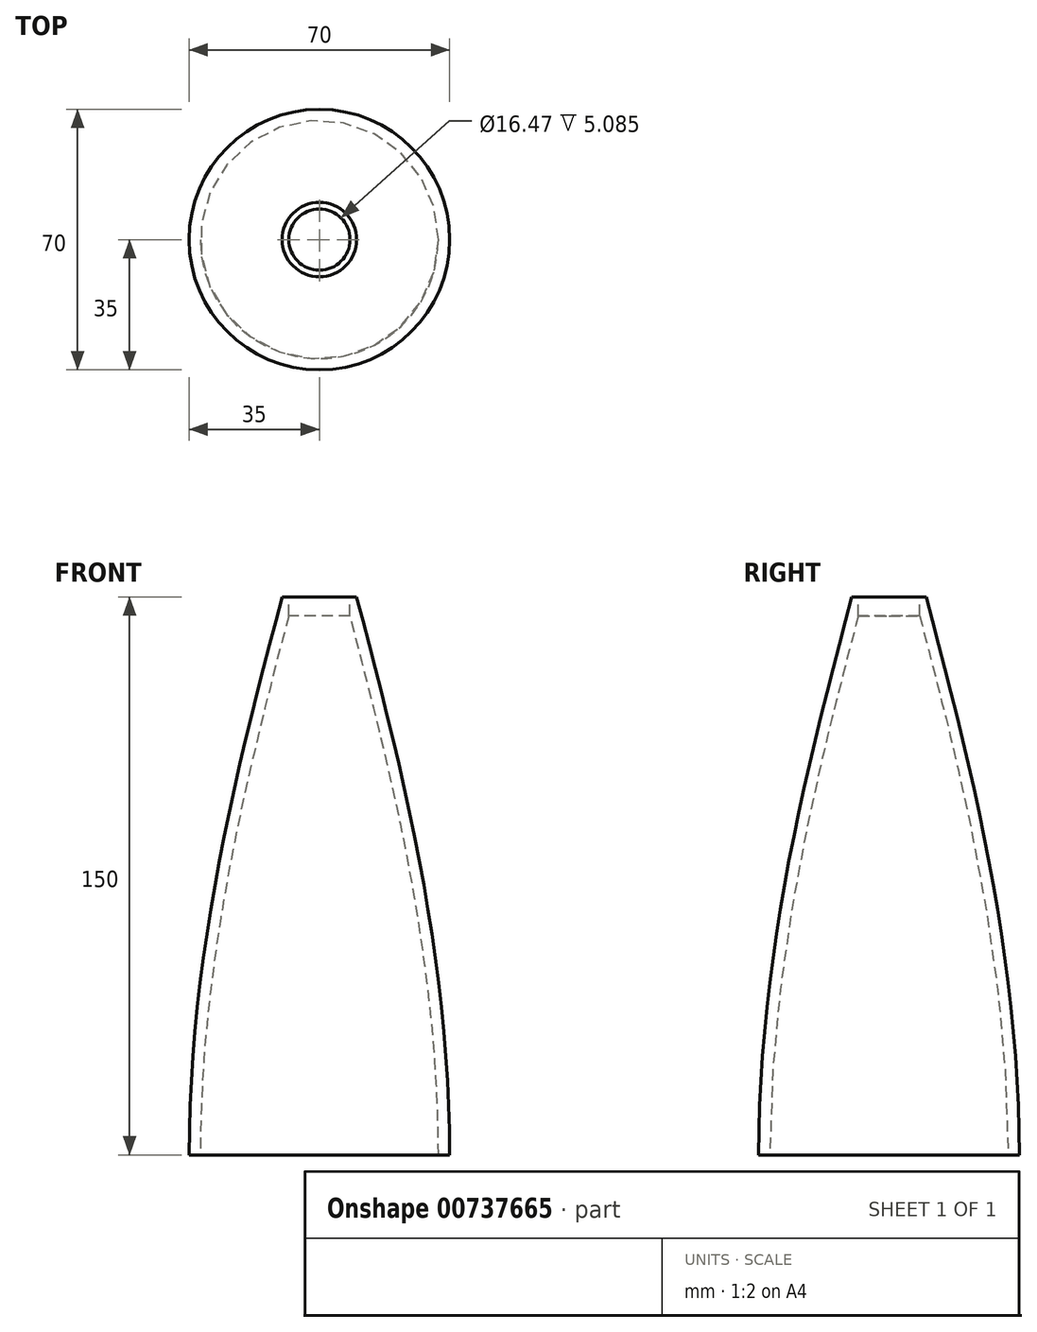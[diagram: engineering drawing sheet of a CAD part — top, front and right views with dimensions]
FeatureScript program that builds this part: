
annotation { "Feature Type Name" : "Feature", "Feature Type Description" : "" }
export const myFeature = defineFeature(function(context is Context, id is Id, definition is map)
    precondition{}
    {
        {
            var Q0;
            Q0=qCreatedBy(makeId("Top.planeOp"),FACE);
            var sketch = newSketch(context, id + "F0", { "sketchPlane" : qUnion([Q0])});
            skCircle(sketch, "E0", {"center": v(0, 0) * mm, "radius": 35 * mm});
            skSolve(sketch);
        }
        {
            var Q0;
            Q0=qCreatedBy(makeId("Top.planeOp"),FACE);
            cPlane(context, id + "F1", {"entities" : qUnion([Q0]), "cplaneType" : CPlaneType.OFFSET, "offset" : 100 * mm, "width" : 150 * mm, "height" : 150 * mm});
        }
        {
            var Q0;
            Q0=qCreatedBy(id+"F1.planeOp",FACE);
            var sketch = newSketch(context, id + "F2", { "sketchPlane" : qUnion([Q0])});
            skCircle(sketch, "E1", {"center": v(0, 0) * mm, "radius": 22.5 * mm});
            skSolve(sketch);
        }
        {
            var Q0;
            Q0=qCreatedBy(id+"F1.planeOp",FACE);
            cPlane(context, id + "F3", {"entities" : qUnion([Q0]), "cplaneType" : CPlaneType.OFFSET, "offset" : 50 * mm, "width" : 150 * mm, "height" : 150 * mm});
        }
        {
            var Q0;
            Q0=qCreatedBy(id+"F3.planeOp",FACE);
            var sketch = newSketch(context, id + "F4", { "sketchPlane" : qUnion([Q0])});
            skCircle(sketch, "E2", {"center": v(0, 0) * mm, "radius": 10 * mm});
            skSolve(sketch);
        }
        {
            var Q0;
            Q0=makeQuery(id+"F0.imprint","IMPRINT",FACE,{"disambiguationData":[TD([[makeQuery(id+"F0.imprint","IMPRINT",EDGE,{"derivedFrom":sQuery(id+"F0.wireOp",EDGE,"E0")}),1.0]])]});
            var Q1;
            Q1=makeQuery(id+"F2.imprint","IMPRINT",FACE,{"disambiguationData":[TD([[makeQuery(id+"F2.imprint","IMPRINT",EDGE,{"derivedFrom":sQuery(id+"F2.wireOp",EDGE,"E1")}),1.0]])]});
            var Q2;
            Q2=makeQuery(id+"F4.imprint","IMPRINT",FACE,{"disambiguationData":[TD([[makeQuery(id+"F4.imprint","IMPRINT",EDGE,{"derivedFrom":sQuery(id+"F4.wireOp",EDGE,"E2")}),1.0]])]});
            loft(context, id + "F5", {"startCondition" : LoftEndDerivativeType.NORMAL_TO_PROFILE, "startMagnitude" : 1, "sheetProfilesArray" : [{ "sheetProfileEntities" : qUnion([Q0]) }, { "sheetProfileEntities" : qUnion([Q1]) }, { "sheetProfileEntities" : qUnion([Q2]) }]});
        }
        {
            var Q0;
            Q0=makeQuery(id+"F5.opLoft","CAP_FACE",FACE,{"disambiguationData":[OSD([makeQuery(id+"F4.imprint","IMPRINT",FACE,{"disambiguationData":[TD([[makeQuery(id+"F4.imprint","IMPRINT",EDGE,{"derivedFrom":sQuery(id+"F4.wireOp",EDGE,"E2")}),1.0]])]})])],"isStart":true});
            var sketch = newSketch(context, id + "F6", { "sketchPlane" : qUnion([Q0])});
            skCircle(sketch, "E3", {"center": v(0, 0) * mm, "radius": 8.23 * mm});
            skSolve(sketch);
        }
        {
            var Q0;
            Q0=makeQuery(id+"F5.opLoft","CAP_FACE",FACE,{"disambiguationData":[OSD([makeQuery(id+"F0.imprint","IMPRINT",FACE,{"disambiguationData":[TD([[makeQuery(id+"F0.imprint","IMPRINT",EDGE,{"derivedFrom":sQuery(id+"F0.wireOp",EDGE,"E0")}),1.0]])]})])],"isStart":true});
            shell(context, id + "F7", {"entities" : qUnion([Q0]), "thickness" : 3 * mm});
        }
        {
            var Q0;
            Q0 = qSketchRegion(id + "F6", true);
            extrude(context, id + "F8", {"entities" : qUnion([Q0]), "operationType" : NewBodyOperationType.REMOVE, "oppositeDirection" : true, "depth" : 25 * mm, "offsetDistance" : 25 * mm});
        }
    });
